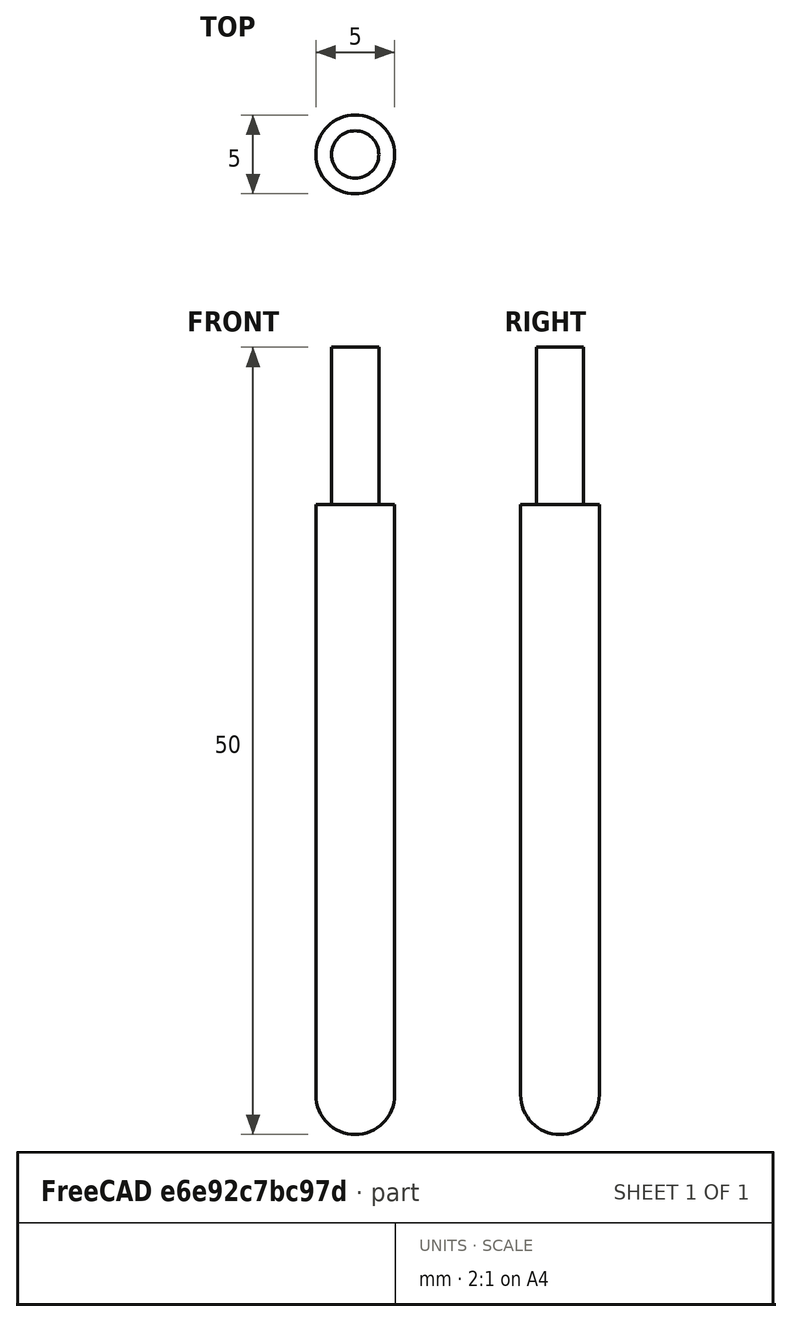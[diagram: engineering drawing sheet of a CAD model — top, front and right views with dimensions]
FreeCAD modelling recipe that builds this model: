
FCSTD DOCUMENT  (FreeCAD 0.19R20874 (Git))
Label: ballend
License: All rights reserved
LicenseURL: http://en.wikipedia.org/wiki/All_rights_reserved
objects: Sketcher::SketchObject×1, PartDesign::Revolution×1, PartDesign::Body×1
note: 4 computed .brp shape members not serialized (recipe doc carries the construction recipe); baked Part::Feature solids carry a one-line shape summary decoded from their .brp

FEATURE [Sketcher::SketchObject] Sketch
  MapMode = 5
  Placement = pos=(0,0,0) rot=(1,0,0;1.5708rad)
  Support = -> [XZ_Plane]
  sketch-geometry (8):
    g0: LineSegment StartX=0 StartY=50 StartZ=0 EndX=0 EndY=0 EndZ=0
    g1: LineSegment StartX=2.5 StartY=2.5 StartZ=0 EndX=2.5 EndY=40 EndZ=0
    g2: LineSegment StartX=1.5 StartY=50 StartZ=0 EndX=0 EndY=50 EndZ=0
    g3: LineSegment [constr] StartX=2.5 StartY=0 StartZ=0 EndX=-2.5 EndY=0 EndZ=0
    g4: LineSegment StartX=1.5 StartY=40 StartZ=0 EndX=2.5 EndY=40 EndZ=0
    g5: LineSegment StartX=1.5 StartY=50 StartZ=0 EndX=1.5 EndY=40 EndZ=0
    g6: LineSegment [constr] StartX=-1.5 StartY=50 StartZ=0 EndX=1.5 EndY=50 EndZ=0
    g7: ArcOfCircle CenterX=-5e-16 CenterY=2.5 CenterZ=0 NormalX=0 NormalY=0 NormalZ=1 AngleXU=0 Radius=2.5 StartAngle=4.71239 EndAngle=6.28319
  constraints (21):
    c: Vertical(g0)
    c: Vertical(g1)
    c: Horizontal(g2)
    c: DistanceX(g3,g3) = 5  'Diameter; Endmill diameter'
    c: DistanceY(g3,g2) = 50  'Length; Overall length of the endmill'
    c: Horizontal(g4)
    c: Coincident(g1,g4)
    c: Vertical(g5)
    c: Coincident(g2,g5)
    c: Symmetric(g6,g6,g0)
    c: Coincident(g6,g2)
    c: DistanceX(g6,g6) = 3  'ShankDiameter; diameter of the shank'
    c: Coincident(g4,g5)
    c: Tangent(g1,g7) = -1.5708
    c: PointOnObject(g0,g3)
    c: Symmetric(g3,g3,g-2)
    c: Vertical(g3,g1)
    c: Perpendicular(g7,g0) = 4.71239
    c: DistanceY(g0,g1) = 40  'CuttingEdgeHeight'
    c: Coincident(g2,g0)
    c: Coincident(g0,g-1)
FEATURE [PartDesign::Revolution] Revolution
  AllowMultiFace = false
  Angle = 360
  Axis = (0,-2e-16,1)
  Base = (0,0,0)
  Placement = pos=(0,0,0) rot=(1,0,0;1.5708rad)
  Profile = -> Sketch
  ReferenceAxis = -> Sketch [V_Axis]
  Reversed = true
FEATURE [PartDesign::Body] Body  label="Ballend"
  Group = -> [Sketch,Revolution]
  Origin = -> Origin
  Tip = -> Revolution
